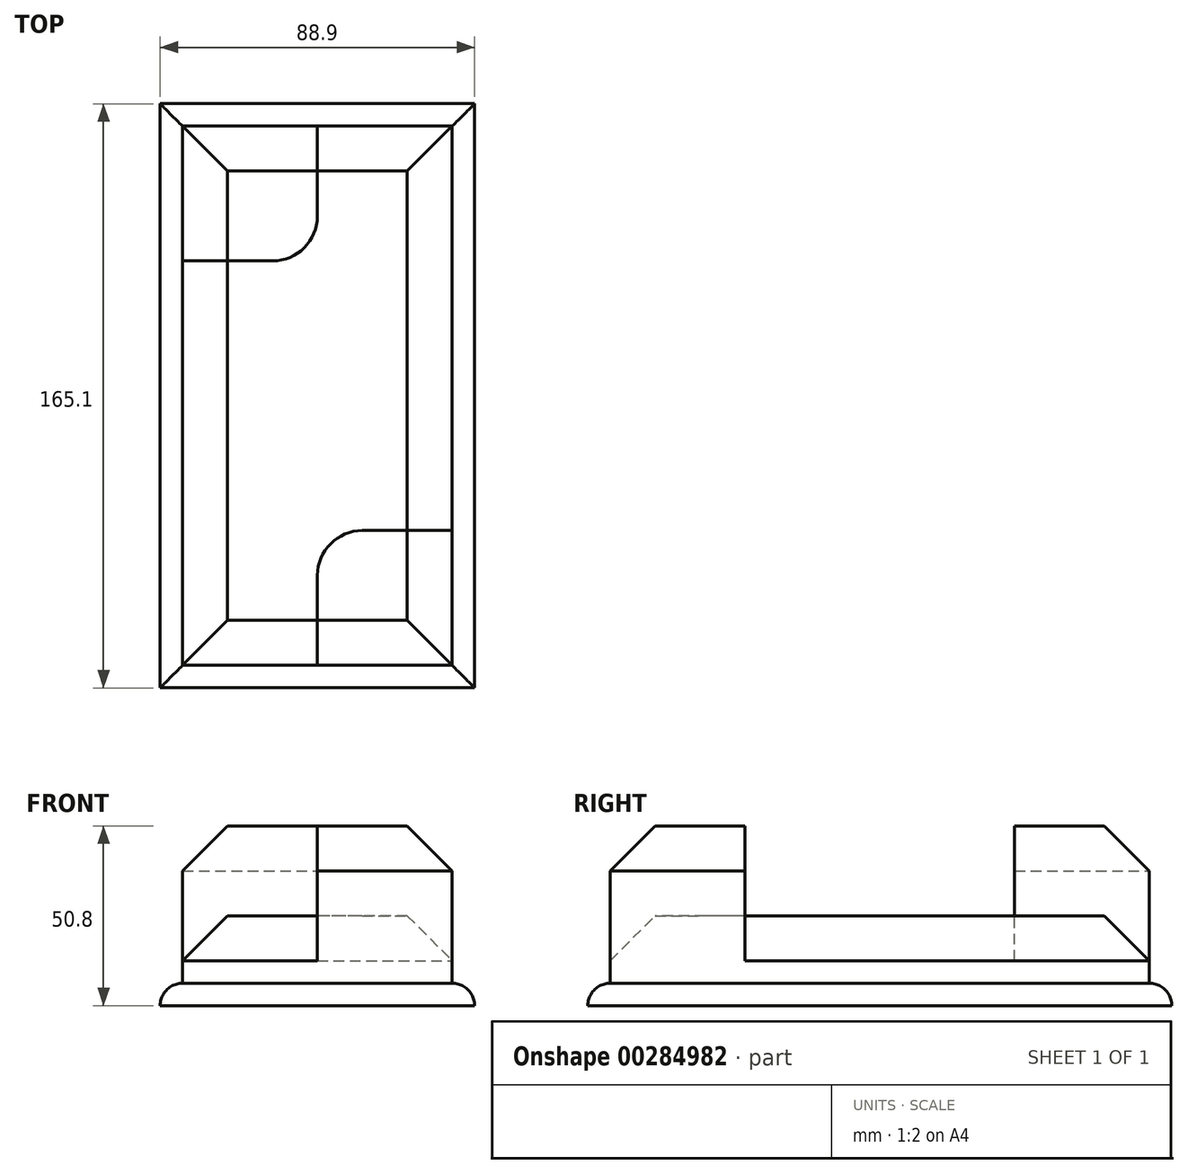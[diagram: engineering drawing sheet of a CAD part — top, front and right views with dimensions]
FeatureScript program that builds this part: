
annotation { "Feature Type Name" : "Feature", "Feature Type Description" : "" }
export const myFeature = defineFeature(function(context is Context, id is Id, definition is map)
    precondition{}
    {
        {
            var Q0;
            Q0=qCreatedBy(makeId("Top.planeOp"),FACE);
            var sketch = newSketch(context, id + "F0", { "sketchPlane" : qUnion([Q0])});
            skLineSegment(sketch, "E0.bottom", {"start": v(-47.6, 93.32) * mm, "end": v(41.3, 93.32) * mm});
            skLineSegment(sketch, "E0.top", {"start": v(-47.6, -71.78) * mm, "end": v(41.3, -71.78) * mm});
            skLineSegment(sketch, "E0.left", {"start": v(-47.6, 93.32) * mm, "end": v(-47.6, -71.78) * mm});
            skLineSegment(sketch, "E0.right", {"start": v(41.3, 93.32) * mm, "end": v(41.3, -71.78) * mm});
            skLineSegment(sketch, "E1.0", {"start": v(-41.26, 86.97) * mm, "end": v(34.94, 86.97) * mm});
            skLineSegment(sketch, "E2.0", {"start": v(34.94, 86.97) * mm, "end": v(34.94, -65.43) * mm});
            skLineSegment(sketch, "E3.0", {"start": v(-41.26, -65.43) * mm, "end": v(34.94, -65.43) * mm});
            skLineSegment(sketch, "E3.1", {"start": v(-41.26, 86.97) * mm, "end": v(-41.26, -65.43) * mm});
            skLineSegment(sketch, "E4", {"start": v(-3.16, -65.43) * mm, "end": v(-3.16, -40.03) * mm});
            skLineSegment(sketch, "E5", {"start": v(9.54, -27.33) * mm, "end": v(34.94, -27.33) * mm});
            skLineSegment(sketch, "E6", {"start": v(-3.16, 86.97) * mm, "end": v(-3.16, 61.57) * mm});
            skLineSegment(sketch, "E7", {"start": v(-15.86, 48.87) * mm, "end": v(-41.26, 48.87) * mm});
            skPoint(sketch, "E8.visualSharp", {"position": v(-3.16, 48.87) * mm});
            skArc(sketch, "E8.filletArc", {"start": v(-15.86, 48.87) * mm, "mid": v(-6.88, 52.6) * mm, "end": v(-3.16, 61.57) * mm});
            skPoint(sketch, "E9.visualSharp", {"position": v(-3.16, -27.33) * mm});
            skArc(sketch, "E9.filletArc", {"start": v(9.54, -27.33) * mm, "mid": v(0.56, -31.05) * mm, "end": v(-3.16, -40.03) * mm});
            skSolve(sketch);
        }
        {
            var Q0;
            Q0=makeQuery(id+"F0.imprint","IMPRINT",FACE,{"disambiguationData":[TD([[makeQuery(id+"F0.imprint","IMPRINT",EDGE,{"derivedFrom":sQuery(id+"F0.wireOp",EDGE,"E0.bottom")}),-1.0]])]});
            extrude(context, id + "F1", {"entities" : qUnion([Q0]), "depth" : 6.35 * mm});
        }
        {
            var Q0;
            Q0=makeQuery(id+"F1.opExtrude","CAP_EDGE",EDGE,{"disambiguationData":[OSD([sQuery(id+"F0.wireOp",EDGE,"E0.left")])],"isStart":false});
            var Q1;
            Q1=makeQuery(id+"F1.opExtrude","CAP_EDGE",EDGE,{"disambiguationData":[OSD([sQuery(id+"F0.wireOp",EDGE,"E0.bottom")])],"isStart":false});
            var Q2;
            Q2=makeQuery(id+"F1.opExtrude","CAP_EDGE",EDGE,{"disambiguationData":[OSD([sQuery(id+"F0.wireOp",EDGE,"E0.right")])],"isStart":false});
            var Q3;
            Q3=makeQuery(id+"F1.opExtrude","CAP_EDGE",EDGE,{"disambiguationData":[OSD([sQuery(id+"F0.wireOp",EDGE,"E0.top")])],"isStart":false});
            fillet(context, id + "F2", {"entities" : qUnion([Q0, Q1, Q2, Q3]), "radius" : 6.35 * mm, "tangentPropagation" : true, "allowEdgeOverflow" : false});
        }
        {
            var Q0;
            {var subQ3=sQuery(id+"F0.wireOp",EDGE,"E4");Q0=makeQuery(id+"F0.imprint","IMPRINT",FACE,{"disambiguationData":[TD([[makeQuery(id+"F0.imprint","IMPRINT",EDGE,{"derivedFrom":subQ3}),1.0]])]});}
            extrude(context, id + "F3", {"entities" : qUnion([Q0]), "operationType" : NewBodyOperationType.ADD, "depth" : 25.4 * mm});
        }
        {
            var Q0;
            Q0=makeQuery(id+"F3.opExtrude","CAP_EDGE",EDGE,{"disambiguationData":[OSD([sQuery(id+"F0.wireOp",EDGE,"E2.0")])],"isStart":false});
            var Q1;
            Q1=makeQuery(id+"F3.opExtrude","CAP_EDGE",EDGE,{"disambiguationData":[OSD([sQuery(id+"F0.wireOp",EDGE,"E1.0")])],"isStart":false});
            var Q2;
            Q2=makeQuery(id+"F3.opExtrude","CAP_EDGE",EDGE,{"disambiguationData":[OSD([sQuery(id+"F0.wireOp",EDGE,"E3.1")])],"isStart":false});
            var Q3;
            Q3=makeQuery(id+"F3.opExtrude","CAP_EDGE",EDGE,{"disambiguationData":[OSD([sQuery(id+"F0.wireOp",EDGE,"E3.0")])],"isStart":false});
            chamfer(context, id + "F4", {"entities" : qUnion([Q0, Q1, Q2, Q3]), "width" : 12.7 * mm, "tangentPropagation" : true});
        }
        {
            var Q0;
            {var subQ4=sQuery(id+"F0.wireOp",EDGE,"E6");Q0=makeQuery(id+"F0.imprint","IMPRINT",FACE,{"disambiguationData":[TD([[makeQuery(id+"F0.imprint","IMPRINT",EDGE,{"derivedFrom":subQ4}),-1.0]])]});}
            var Q1;
            {var subQ4=sQuery(id+"F0.wireOp",EDGE,"E4");Q1=makeQuery(id+"F0.imprint","IMPRINT",FACE,{"disambiguationData":[TD([[makeQuery(id+"F0.imprint","IMPRINT",EDGE,{"derivedFrom":subQ4}),-1.0]])]});}
            extrude(context, id + "F5", {"entities" : qUnion([Q0, Q1]), "operationType" : NewBodyOperationType.ADD, "depth" : 50.8 * mm});
        }
        {
            var Q0;
            Q0=makeQuery(id+"F5.opExtrude","CAP_EDGE",EDGE,{"disambiguationData":[OSD([sQuery(id+"F0.wireOp",EDGE,"E1.0")])],"isStart":false});
            var Q1;
            Q1=makeQuery(id+"F5.opExtrude","CAP_EDGE",EDGE,{"disambiguationData":[OSD([sQuery(id+"F0.wireOp",EDGE,"E3.1")])],"isStart":false});
            var Q2;
            Q2=makeQuery(id+"F5.opExtrude","CAP_EDGE",EDGE,{"disambiguationData":[OSD([sQuery(id+"F0.wireOp",EDGE,"E2.0")])],"isStart":false});
            var Q3;
            Q3=makeQuery(id+"F5.opExtrude","CAP_EDGE",EDGE,{"disambiguationData":[OSD([sQuery(id+"F0.wireOp",EDGE,"E3.0")])],"isStart":false});
            chamfer(context, id + "F6", {"entities" : qUnion([Q0, Q1, Q2, Q3]), "width" : 12.7 * mm, "tangentPropagation" : true});
        }
    });
